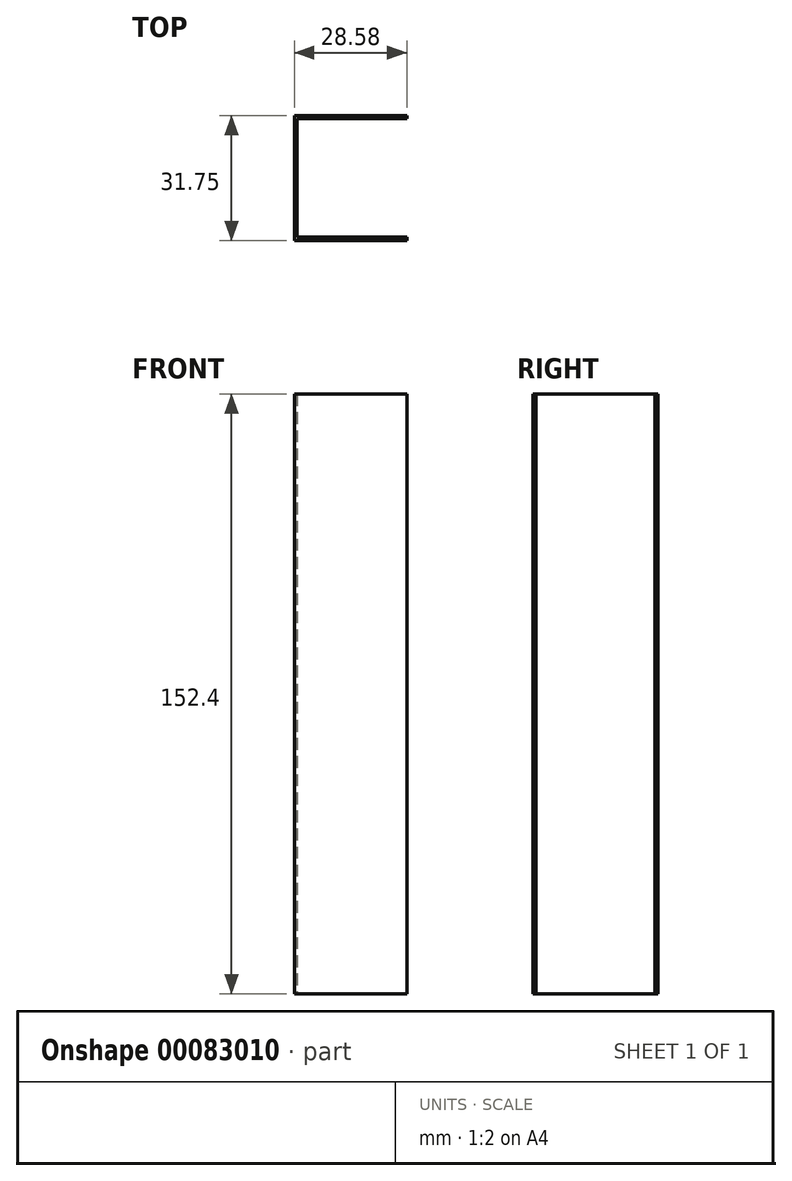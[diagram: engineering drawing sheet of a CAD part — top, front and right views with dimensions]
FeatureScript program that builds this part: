
annotation { "Feature Type Name" : "Feature", "Feature Type Description" : "" }
export const myFeature = defineFeature(function(context is Context, id is Id, definition is map)
    precondition{}
    {
        {
            var Q0;
            Q0=qCreatedBy(makeId("Top.planeOp"),FACE);
            var sketch = newSketch(context, id + "F0", { "sketchPlane" : qUnion([Q0])});
            skLineSegment(sketch, "E0.bottom", {"start": v(-115.14, 60.1) * mm, "end": v(-86.56, 60.1) * mm});
            skLineSegment(sketch, "E0.top", {"start": v(-115.14, 28.35) * mm, "end": v(-86.56, 28.35) * mm});
            skLineSegment(sketch, "E0.left", {"start": v(-115.14, 60.1) * mm, "end": v(-115.14, 28.35) * mm});
            skLineSegment(sketch, "E0.right", {"start": v(-86.56, 60.1) * mm, "end": v(-86.56, 28.35) * mm});
            skLineSegment(sketch, "E1.bottom", {"start": v(-114.5, 29.19) * mm, "end": v(-85.6, 29.19) * mm});
            skLineSegment(sketch, "E1.top", {"start": v(-114.5, 59.32) * mm, "end": v(-85.6, 59.32) * mm});
            skLineSegment(sketch, "E1.left", {"start": v(-114.5, 29.19) * mm, "end": v(-114.5, 59.32) * mm});
            skLineSegment(sketch, "E1.right", {"start": v(-85.6, 29.19) * mm, "end": v(-85.6, 59.32) * mm});
            skSolve(sketch);
        }
        {
            var Q0;
            {var subQ1=sQuery(id+"F0.wireOp",EDGE,"E0.bottom");Q0=makeQuery(id+"F0.imprint","IMPRINT",FACE,{"disambiguationData":[TD([[makeQuery(id+"F0.imprint","IMPRINT",EDGE,{"derivedFrom":subQ1}),-1.0]])]});}
            extrude(context, id + "F1", {"entities" : qUnion([Q0]), "depth" : 152.4 * mm});
        }
    });
